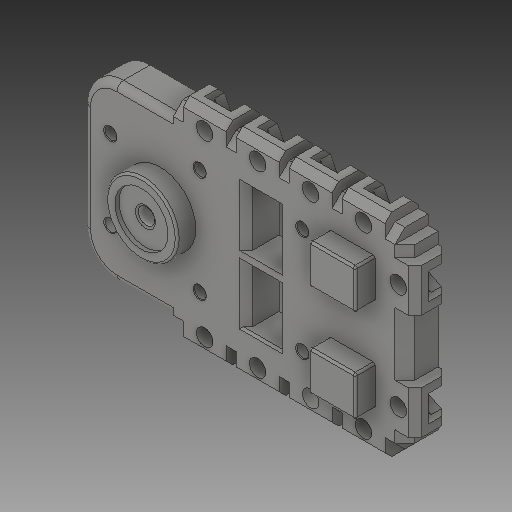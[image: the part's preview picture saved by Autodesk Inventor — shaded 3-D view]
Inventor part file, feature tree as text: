
AUTODESK INVENTOR PART (.ipt)
format: ipt  version: 2018 (Build 220112000, 112)  size: 362,496 bytes
history: native  units: mm
features: other x1, fillet x1
ambient origin geometry x8: Origin, YZ Plane, XZ Plane, XY Plane, X Axis, Y Axis, Z Axis, Center Point
bodies: Body1 (feature_tree)
feature tree (2):
  other  "Твердое тело1"
  fillet  "Fillet3"  [1 undecoded]
note: 1 required parameter value undecoded (feature->parameter linkage not recoverable at this tier; creation-order binding heuristic only, values carry confidence <= 0.55)
